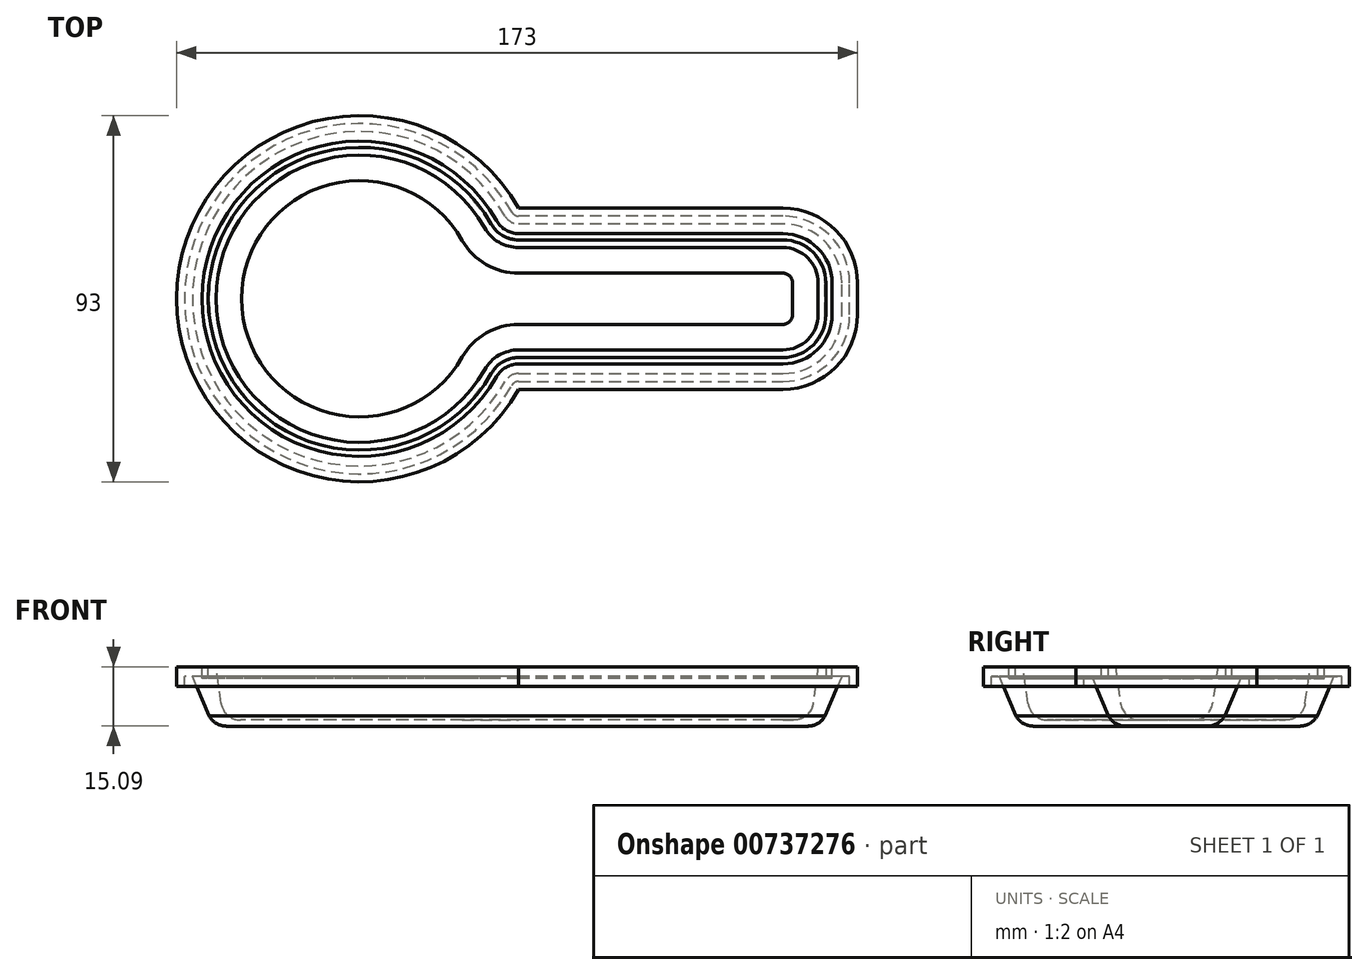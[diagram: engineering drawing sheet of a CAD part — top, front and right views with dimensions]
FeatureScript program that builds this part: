
annotation { "Feature Type Name" : "Feature", "Feature Type Description" : "" }
export const myFeature = defineFeature(function(context is Context, id is Id, definition is map)
    precondition{}
    {
        {
            var Q0;
            Q0=qCreatedBy(makeId("Front.planeOp"),FACE);
            var sketch = newSketch(context, id + "F0", { "sketchPlane" : qUnion([Q0])});
            skPoint(sketch, "E0.third.point", {"position": v(373, -204.53) * mm});
            skLineSegment(sketch, "E1", {"start": v(-33.5, -0.06) * mm, "end": v(-30, -0.06) * mm});
            skLineSegment(sketch, "E2", {"start": v(-30, -0.06) * mm, "end": v(-33.82, -0.1) * mm});
            skLineSegment(sketch, "E3", {"start": v(-36.5, 15) * mm, "end": v(-35.2, 5.74) * mm});
            skArc(sketch, "E4.filletArc", {"start": v(-35.2, 5.74) * mm, "mid": v(-33.43, 2.58) * mm, "end": v(-30, 1.44) * mm});
            skArc(sketch, "E5.filletArc", {"start": v(-38.26, 2.52) * mm, "mid": v(-36.4, 0.6) * mm, "end": v(-33.82, -0.1) * mm});
            skLineSegment(sketch, "E6", {"start": v(-46.5, 15) * mm, "end": v(-46.5, 10) * mm});
            skLineSegment(sketch, "E7", {"start": v(-46.5, 10) * mm, "end": v(-44.5, 10) * mm});
            skLineSegment(sketch, "E8", {"start": v(-44.5, 10) * mm, "end": v(-44.5, 12.5) * mm});
            skLineSegment(sketch, "E9", {"start": v(-44.5, 12.5) * mm, "end": v(-42.5, 12.5) * mm});
            skLineSegment(sketch, "E10", {"start": v(-42.5, 12.5) * mm, "end": v(-38.26, 2.52) * mm});
            skLineSegment(sketch, "E11", {"start": v(-30, 1.44) * mm, "end": v(-30, -0.06) * mm});
            skLineSegment(sketch, "E12", {"start": v(-38.45, 15) * mm, "end": v(-38.45, 12) * mm});
            skLineSegment(sketch, "E13", {"start": v(-38.45, 12) * mm, "end": v(-40.05, 12) * mm});
            skLineSegment(sketch, "E14", {"start": v(-40.05, 12) * mm, "end": v(-40.05, 15) * mm});
            skLineSegment(sketch, "E15.trimOffspring", {"start": v(-38.45, 15) * mm, "end": v(-36.5, 15) * mm});
            skLineSegment(sketch, "E16", {"start": v(-46.5, 15) * mm, "end": v(-40.05, 15) * mm});
            skSolve(sketch);
        }
        {
            var Q0;
            Q0=qCreatedBy(makeId("Top.planeOp"),FACE);
            var sketch = newSketch(context, id + "F1", { "sketchPlane" : qUnion([Q0])});
            skLineSegment(sketch, "E17", {"start": v(107.5, -6.5) * mm, "end": v(40.41, -6.5) * mm});
            skLineSegment(sketch, "E18", {"start": v(107.5, 6.5) * mm, "end": v(40.41, 6.5) * mm});
            skArc(sketch, "E19.filletArc", {"start": v(26.07, 14.84) * mm, "mid": v(32.12, 8.74) * mm, "end": v(40.41, 6.5) * mm});
            skArc(sketch, "E20.filletArc", {"start": v(40.41, -6.5) * mm, "mid": v(32.12, -8.74) * mm, "end": v(26.07, -14.84) * mm});
            skArc(sketch, "E21.converted", {"start": v(26.07, 14.84) * mm, "mid": v(-30, 0) * mm, "end": v(26.07, -14.84) * mm});
            skLineSegment(sketch, "E22", {"start": v(110, 4) * mm, "end": v(110, -4) * mm});
            skPoint(sketch, "E23.visualSharp", {"position": v(110, 6.5) * mm});
            skArc(sketch, "E23.filletArc", {"start": v(110, 4) * mm, "mid": v(109.27, 5.77) * mm, "end": v(107.5, 6.5) * mm});
            skPoint(sketch, "E24.visualSharp", {"position": v(110, -6.5) * mm});
            skArc(sketch, "E24.filletArc", {"start": v(107.5, -6.5) * mm, "mid": v(109.27, -5.77) * mm, "end": v(110, -4) * mm});
            skSolve(sketch);
        }
        {
            var Q0;
            Q0=makeQuery(id+"F0.imprint","IMPRINT",FACE,{"disambiguationData":[TD([[makeQuery(id+"F0.imprint","IMPRINT",EDGE,{"derivedFrom":sQuery(id+"F0.wireOp",EDGE,"E2")}),-1.0]])]});
            var Q1;
            Q1=sQuery(id+"F1.wireOp",EDGE,"E24.filletArc");
            var Q2;
            Q2=sQuery(id+"F1.wireOp",EDGE,"E22");
            var Q3;
            Q3=sQuery(id+"F1.wireOp",EDGE,"E23.filletArc");
            var Q4;
            Q4=sQuery(id+"F1.wireOp",EDGE,"E18");
            var Q5;
            Q5=sQuery(id+"F1.wireOp",EDGE,"E17");
            var Q6;
            Q6=sQuery(id+"F1.wireOp",EDGE,"E21.converted");
            var Q7;
            Q7=sQuery(id+"F1.wireOp",EDGE,"E20.filletArc");
            var Q8;
            Q8=sQuery(id+"F1.wireOp",EDGE,"E19.filletArc");
            sweep(context, id + "F2", {"profiles" : qUnion([Q0]), "path" : qUnion([Q1, Q2, Q3, Q4, Q5, Q6, Q7, Q8])});
        }
        {
            var Q0;
            Q0=makeQuery(id+"F1.imprint","IMPRINT",FACE,{"disambiguationData":[TD([[makeQuery(id+"F1.imprint","IMPRINT",EDGE,{"derivedFrom":sQuery(id+"F1.wireOp",EDGE,"E17")}),-1.0]])]});
            extrude(context, id + "F3", {"entities" : qUnion([Q0]), "operationType" : NewBodyOperationType.ADD, "depth" : 1.5 * mm, "offsetDistance" : 25 * mm});
        }
    });
